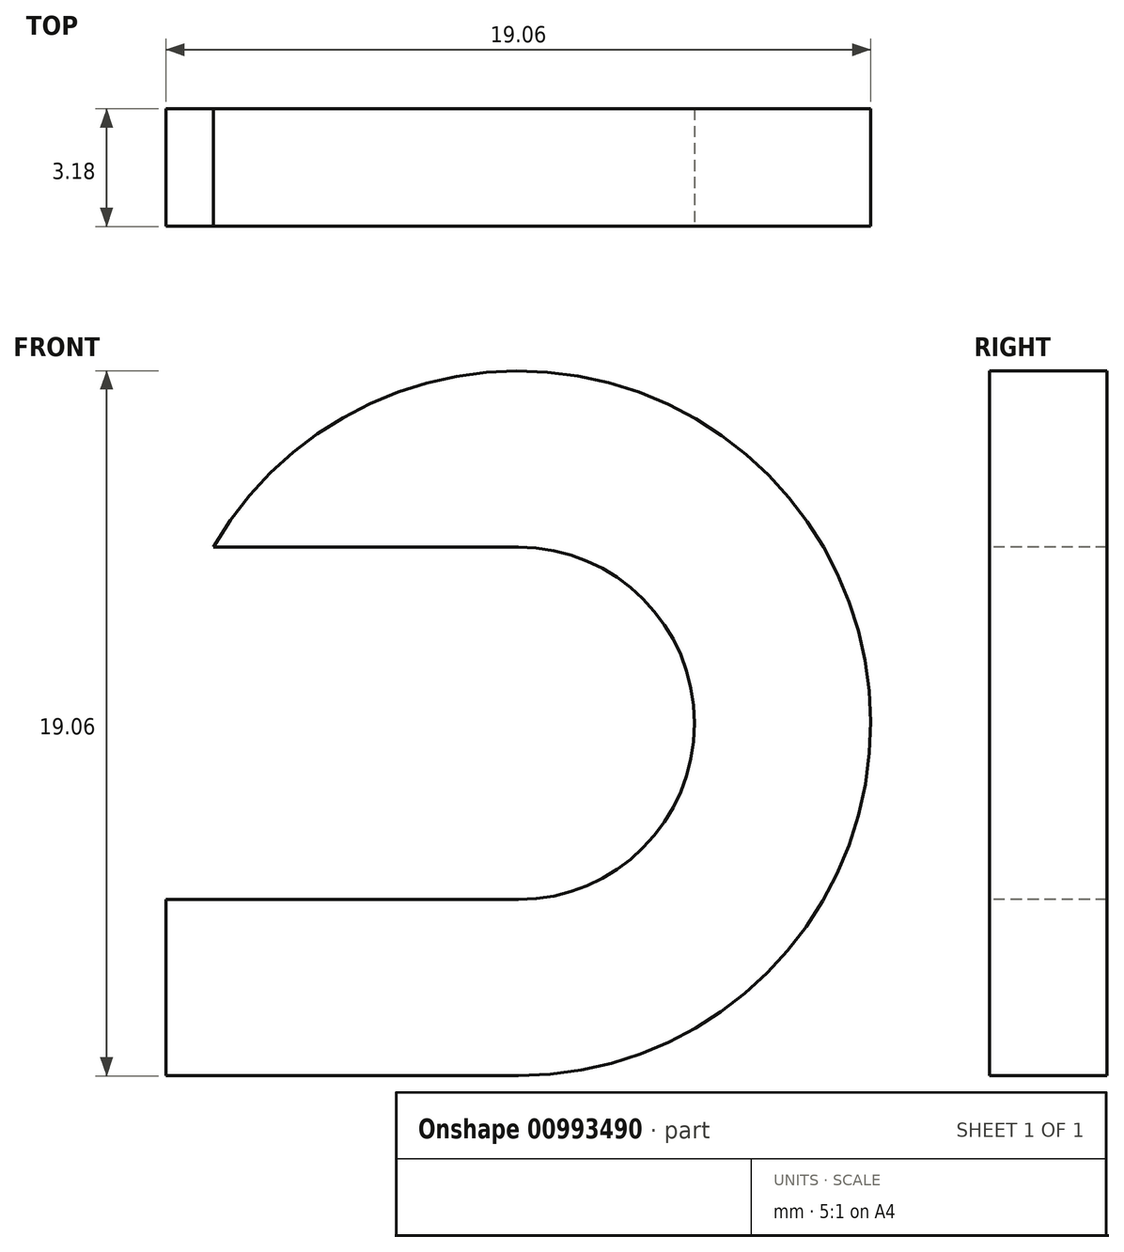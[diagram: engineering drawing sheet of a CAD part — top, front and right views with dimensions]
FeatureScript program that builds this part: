
annotation { "Feature Type Name" : "Feature", "Feature Type Description" : "" }
export const myFeature = defineFeature(function(context is Context, id is Id, definition is map)
    precondition{}
    {
        {
            var Q0;
            Q0=qCreatedBy(makeId("Front.planeOp"),FACE);
            var sketch = newSketch(context, id + "F0", { "sketchPlane" : qUnion([Q0])});
            skLineSegment(sketch, "E0.bottom", {"start": v(9.53, -9.52) * mm, "end": v(-9.53, -9.53) * mm});
            skLineSegment(sketch, "E0.top", {"start": v(9.53, 9.53) * mm, "end": v(-9.53, 9.53) * mm});
            skLineSegment(sketch, "E0.left", {"start": v(9.53, -9.52) * mm, "end": v(9.53, 9.53) * mm});
            skLineSegment(sketch, "E0.right", {"start": v(-9.53, -9.53) * mm, "end": v(-9.53, 9.53) * mm});
            skPoint(sketch, "E0.middle", {"position": v(0, 0) * mm});
            skSolve(sketch);
        }
        {
            var Q0;
            Q0=makeQuery(id+"F0.imprint","IMPRINT",FACE,{"disambiguationData":[TD([[makeQuery(id+"F0.imprint","IMPRINT",EDGE,{"derivedFrom":sQuery(id+"F0.wireOp",EDGE,"E0.bottom")}),-1.0]])]});
            extrude(context, id + "F1", {"entities" : qUnion([Q0]), "depth" : 3.17 * mm, "offsetDistance" : 25.4 * mm});
        }
        {
            var Q0;
            Q0=makeQuery(id+"F1.opExtrude","CAP_FACE",FACE,{"disambiguationData":[OSD([sQuery(id+"F0.wireOp",EDGE,"E0.bottom"),sQuery(id+"F0.wireOp",EDGE,"E0.top"),sQuery(id+"F0.wireOp",EDGE,"E0.left"),sQuery(id+"F0.wireOp",EDGE,"E0.right")])],"isStart":false});
            var sketch = newSketch(context, id + "F2", { "sketchPlane" : qUnion([Q0])});
            skCircle(sketch, "E1", {"center": v(0, 0) * mm, "radius": 4.76 * mm});
            skLineSegment(sketch, "E2", {"start": v(0, -4.76) * mm, "end": v(-9.52, -4.76) * mm});
            skLineSegment(sketch, "E3", {"start": v(0, 4.76) * mm, "end": v(-9.53, 4.76) * mm});
            skLineSegment(sketch, "E4", {"start": v(-9.52, 4.76) * mm, "end": v(-9.52, -4.76) * mm});
            skSolve(sketch);
        }
        {
            var Q0;
            {var subQ0=sQuery(id+"F2.wireOp",EDGE,"E1");var subQ1=makeQuery(id+"F2.imprint","INTERSECT",VERTEX,{"derivedFrom":[subQ0,sQuery(id+"F2.wireOp",EDGE,"E2")]});Q0=makeQuery(id+"F2.imprint","IMPRINT",FACE,{"disambiguationData":[TD([[makeQuery(id+"F2.imprint","IMPRINT",EDGE,{"disambiguationData":[TD([[subQ1,1.0]])],"derivedFrom":subQ0}),1.0]])]});}
            var Q1;
            {var subQ0=sQuery(id+"F2.wireOp",EDGE,"E2");Q1=makeQuery(id+"F2.imprint","IMPRINT",FACE,{"disambiguationData":[TD([[makeQuery(id+"F2.imprint","IMPRINT",EDGE,{"derivedFrom":subQ0}),-1.0]])]});}
            extrude(context, id + "F3", {"entities" : qUnion([Q0, Q1]), "operationType" : NewBodyOperationType.REMOVE, "oppositeDirection" : true, "depth" : 25.4 * mm, "offsetDistance" : 25.4 * mm});
        }
        {
            var Q0;
            Q0=makeQuery(id+"F1.opExtrude","CAP_FACE",FACE,{"disambiguationData":[OSD([sQuery(id+"F0.wireOp",EDGE,"E0.bottom"),sQuery(id+"F0.wireOp",EDGE,"E0.top"),sQuery(id+"F0.wireOp",EDGE,"E0.left"),sQuery(id+"F0.wireOp",EDGE,"E0.right")])],"isStart":false});
            var sketch = newSketch(context, id + "F4", { "sketchPlane" : qUnion([Q0])});
            skCircle(sketch, "E5", {"center": v(0, 0) * mm, "radius": 9.53 * mm});
            skSolve(sketch);
        }
        {
            var Q0;
            {var subQ0=sQuery(id+"F4.wireOp",EDGE,"E5");var subQ1=sQuery(id+"F0.wireOp",EDGE,"E0.top");var subQ2=makeQuery(id+"F1.opExtrude","CAP_EDGE",EDGE,{"disambiguationData":[OSD([subQ1])],"isStart":false});var subQ3=makeQuery(id+"F4.imprint","INTERSECT",VERTEX,{"derivedFrom":[subQ2,subQ0]});Q0=makeQuery(id+"F4.imprint","IMPRINT",FACE,{"disambiguationData":[TD([[makeQuery(id+"F4.imprint","IMPRINT",EDGE,{"disambiguationData":[TD([[subQ3,-1.0]])],"derivedFrom":subQ0}),-1.0]])]});}
            var Q1;
            {var subQ0=sQuery(id+"F4.wireOp",EDGE,"E5");var subQ1=makeQuery(id+"F1.opExtrude","CAP_EDGE",EDGE,{"disambiguationData":[OSD([sQuery(id+"F0.wireOp",EDGE,"E0.top")])],"isStart":false});var subQ2=makeQuery(id+"F4.imprint","INTERSECT",VERTEX,{"derivedFrom":[subQ1,subQ0]});Q1=makeQuery(id+"F4.imprint","IMPRINT",FACE,{"disambiguationData":[TD([[makeQuery(id+"F4.imprint","IMPRINT",EDGE,{"disambiguationData":[TD([[subQ2,1.0]])],"derivedFrom":subQ0}),-1.0]])]});}
            var Q2;
            {var subQ0=sQuery(id+"F4.wireOp",EDGE,"E5");var subQ1=makeQuery(id+"F1.opExtrude","CAP_EDGE",EDGE,{"disambiguationData":[OSD([sQuery(id+"F0.wireOp",EDGE,"E0.left")])],"isStart":false});var subQ2=makeQuery(id+"F4.imprint","INTERSECT",VERTEX,{"derivedFrom":[subQ1,subQ0]});Q2=makeQuery(id+"F4.imprint","IMPRINT",FACE,{"disambiguationData":[TD([[makeQuery(id+"F4.imprint","IMPRINT",EDGE,{"disambiguationData":[TD([[subQ2,1.0]])],"derivedFrom":subQ0}),-1.0]])]});}
            var Q3;
            {var subQ0=sQuery(id+"F4.wireOp",EDGE,"E5");var subQ1=sQuery(id+"F2.wireOp",EDGE,"E2");var subQ2=makeQuery(id+"F3.boolean.opBoolean","COPY",EDGE,{"derivedFrom":makeQuery(id+"F3.opExtrude","CAP_EDGE",EDGE,{"disambiguationData":[OSD([subQ1])],"isStart":true})});var subQ3=makeQuery(id+"F4.imprint","INTERSECT",VERTEX,{"derivedFrom":[subQ2,subQ0]});Q3=makeQuery(id+"F4.imprint","IMPRINT",FACE,{"disambiguationData":[TD([[makeQuery(id+"F4.imprint","IMPRINT",EDGE,{"disambiguationData":[TD([[subQ3,-1.0]])],"derivedFrom":subQ0}),-1.0]])]});}
            extrude(context, id + "F5", {"entities" : qUnion([Q0, Q1, Q2, Q3]), "operationType" : NewBodyOperationType.REMOVE, "oppositeDirection" : true, "depth" : 25.4 * mm, "offsetDistance" : 25.4 * mm});
        }
    });
